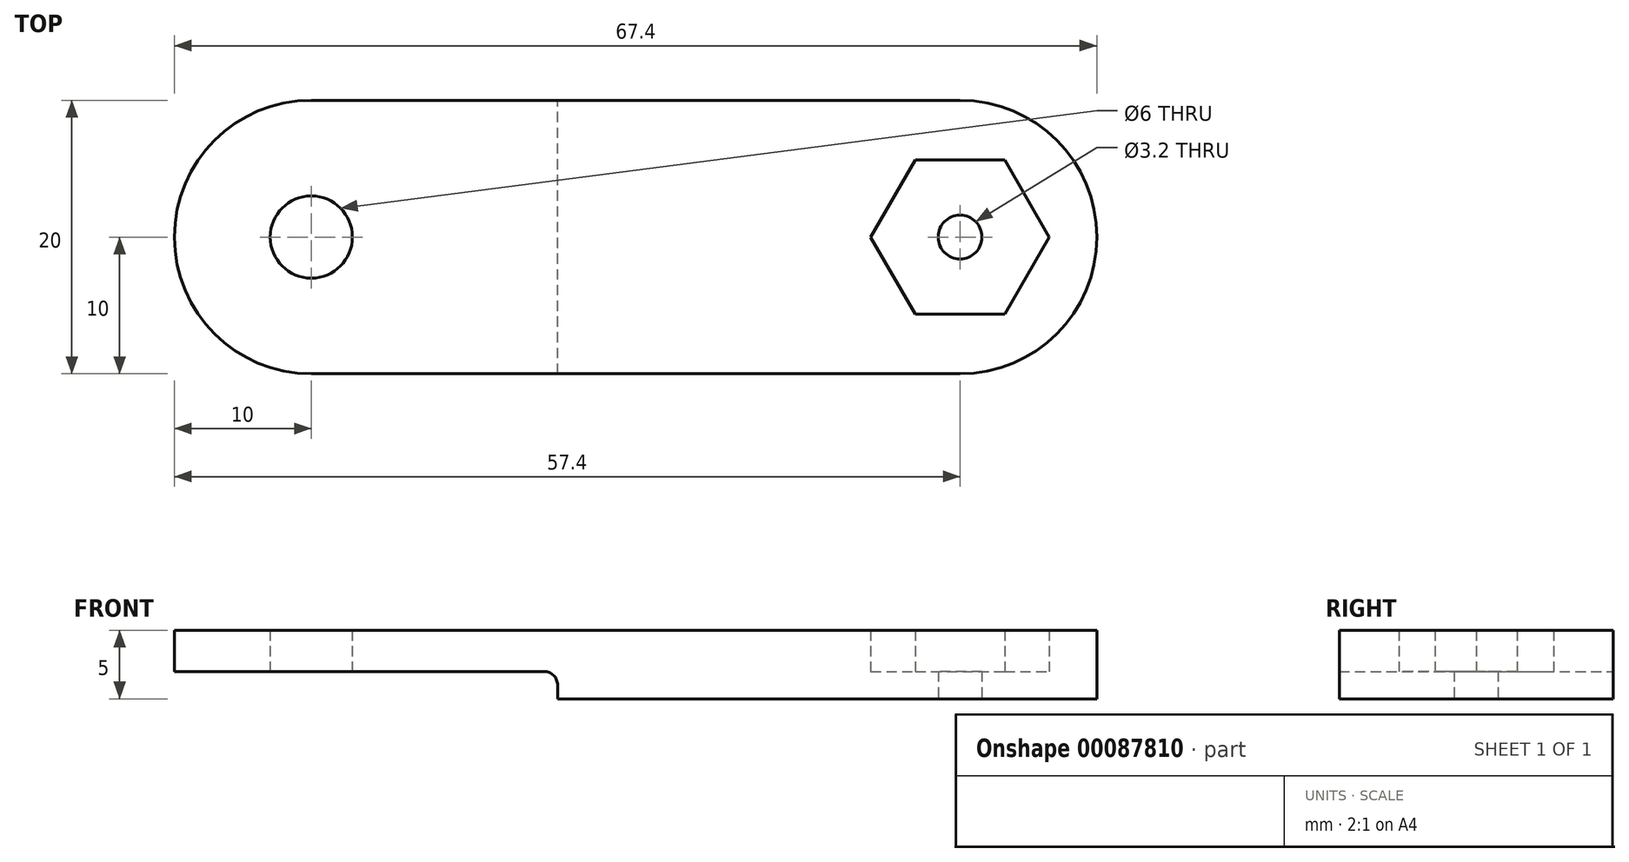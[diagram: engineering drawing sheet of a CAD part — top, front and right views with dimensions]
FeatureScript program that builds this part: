
annotation { "Feature Type Name" : "Feature", "Feature Type Description" : "" }
export const myFeature = defineFeature(function(context is Context, id is Id, definition is map)
    precondition{}
    {
        {
            var Q0;
            Q0=qCreatedBy(makeId("Top.planeOp"),FACE);
            var sketch = newSketch(context, id + "F0", { "sketchPlane" : qUnion([Q0])});
            skArc(sketch, "E0", {"start": v(0, -10) * mm, "mid": v(10, 0) * mm, "end": v(0, 10) * mm});
            skLineSegment(sketch, "E1", {"start": v(0, 10) * mm, "end": v(-47.4, 10) * mm});
            skLineSegment(sketch, "E2", {"start": v(0, -10) * mm, "end": v(-47.4, -10) * mm});
            skArc(sketch, "E3", {"start": v(-47.4, 10) * mm, "mid": v(-57.4, 0) * mm, "end": v(-47.4, -10) * mm});
            skPoint(sketch, "E3.second.point", {"position": v(-47.4, 10) * mm});
            skPoint(sketch, "E3.third.point", {"position": v(-56.72, 3.63) * mm});
            skCircle(sketch, "E4", {"center": v(-47.4, 0) * mm, "radius": 3 * mm});
            skCircle(sketch, "E5.cCircle", {"center": v(0, 0) * mm, "radius": 5.65 * mm, "construction": true});
            skLineSegment(sketch, "E5.0", {"start": v(-3.26, 5.65) * mm, "end": v(3.26, 5.65) * mm});
            skLineSegment(sketch, "E5.1", {"start": v(3.26, 5.65) * mm, "end": v(6.52, 0) * mm});
            skLineSegment(sketch, "E5.2", {"start": v(6.52, 0) * mm, "end": v(3.26, -5.65) * mm});
            skLineSegment(sketch, "E5.3", {"start": v(3.26, -5.65) * mm, "end": v(-3.26, -5.65) * mm});
            skLineSegment(sketch, "E5.4", {"start": v(-3.26, -5.65) * mm, "end": v(-6.52, 0) * mm});
            skLineSegment(sketch, "E5.5", {"start": v(-6.52, 0) * mm, "end": v(-3.26, 5.65) * mm});
            skPoint(sketch, "E5.0.midPoint", {"position": v(0, 5.65) * mm});
            skCircle(sketch, "E6", {"center": v(0, 0) * mm, "radius": 1.6 * mm});
            skSolve(sketch);
        }
        {
            var Q0;
            Q0 = qSketchRegion(id + "F0", true);
            extrude(context, id + "F1", {"entities" : qUnion([Q0]), "depth" : 5 * mm});
        }
        {
            var Q0;
            Q0=makeQuery(id+"F0.imprint","IMPRINT",FACE,{"disambiguationData":[TD([[makeQuery(id+"F0.imprint","IMPRINT",EDGE,{"derivedFrom":sQuery(id+"F0.wireOp",EDGE,"E5.0")}),-1.0]])]});
            extrude(context, id + "F2", {"entities" : qUnion([Q0]), "operationType" : NewBodyOperationType.ADD, "depth" : 2 * mm});
        }
        {
            var Q0;
            Q0=makeQuery(id+"F1.opExtrude","CAP_FACE",FACE,{"disambiguationData":[OSD([sQuery(id+"F0.wireOp",EDGE,"E0"),sQuery(id+"F0.wireOp",EDGE,"E1"),sQuery(id+"F0.wireOp",EDGE,"E2"),sQuery(id+"F0.wireOp",EDGE,"E3"),sQuery(id+"F0.wireOp",EDGE,"E4"),sQuery(id+"F0.wireOp",EDGE,"E5.0"),sQuery(id+"F0.wireOp",EDGE,"E5.1"),sQuery(id+"F0.wireOp",EDGE,"E5.2"),sQuery(id+"F0.wireOp",EDGE,"E5.3"),sQuery(id+"F0.wireOp",EDGE,"E5.4"),sQuery(id+"F0.wireOp",EDGE,"E5.5")])],"isStart":false});
            var sketch = newSketch(context, id + "F3", { "sketchPlane" : qUnion([Q0])});
            skLineSegment(sketch, "E7.bottom", {"start": v(-29.4, 10) * mm, "end": v(-59.4, 10) * mm});
            skLineSegment(sketch, "E7.top", {"start": v(-29.4, -10) * mm, "end": v(-59.4, -10) * mm});
            skLineSegment(sketch, "E7.left", {"start": v(-29.4, 10) * mm, "end": v(-29.4, -10) * mm});
            skLineSegment(sketch, "E7.right", {"start": v(-59.4, 10) * mm, "end": v(-59.4, -10) * mm});
            skLineSegment(sketch, "E8", {"start": v(-47.4, 0) * mm, "end": v(-47.4, 10) * mm, "construction": true});
            skSolve(sketch);
        }
        {
            var Q0;
            {var subQ0=sQuery(id+"F0.wireOp",EDGE,"E5.5");var subQ1=sQuery(id+"F0.wireOp",EDGE,"E5.4");var subQ2=sQuery(id+"F0.wireOp",EDGE,"E5.3");var subQ3=sQuery(id+"F0.wireOp",EDGE,"E5.2");var subQ4=sQuery(id+"F0.wireOp",EDGE,"E5.1");var subQ5=sQuery(id+"F0.wireOp",EDGE,"E5.0");Q0=makeQuery(id+"F2.boolean.opBoolean","MERGE",FACE,{"derivedFrom":[makeQuery(id+"F1.opExtrude","CAP_FACE",FACE,{"disambiguationData":[OSD([sQuery(id+"F0.wireOp",EDGE,"E0"),sQuery(id+"F0.wireOp",EDGE,"E1"),sQuery(id+"F0.wireOp",EDGE,"E2"),sQuery(id+"F0.wireOp",EDGE,"E3"),sQuery(id+"F0.wireOp",EDGE,"E4"),subQ5,subQ4,subQ3,subQ2,subQ1,subQ0])],"isStart":true}),makeQuery(id+"F2.opExtrude","CAP_FACE",FACE,{"disambiguationData":[OSD([subQ5,subQ4,subQ3,subQ2,subQ1,subQ0,sQuery(id+"F0.wireOp",EDGE,"E6")])],"isStart":true})]});}
            var sketch = newSketch(context, id + "F4", { "sketchPlane" : qUnion([Q0])});
            skLineSegment(sketch, "E9.bottom", {"start": v(-29.4, 10) * mm, "end": v(-59.4, 10) * mm});
            skLineSegment(sketch, "E9.top", {"start": v(-29.4, -10) * mm, "end": v(-59.4, -10) * mm});
            skLineSegment(sketch, "E9.left", {"start": v(-29.4, 10) * mm, "end": v(-29.4, -10) * mm});
            skLineSegment(sketch, "E9.right", {"start": v(-59.4, 10) * mm, "end": v(-59.4, -10) * mm});
            skSolve(sketch);
        }
        {
            var Q0;
            Q0 = qSketchRegion(id + "F4", true);
            extrude(context, id + "F5", {"entities" : qUnion([Q0]), "operationType" : NewBodyOperationType.REMOVE, "oppositeDirection" : true, "depth" : 2 * mm});
        }
        {
            var Q0;
            Q0=makeQuery(id+"F5.boolean.opBoolean","COPY",EDGE,{"derivedFrom":makeQuery(id+"F5.opExtrude","CAP_EDGE",EDGE,{"disambiguationData":[OSD([sQuery(id+"F4.wireOp",EDGE,"E9.left")])],"isStart":false})});
            var Q1;
            Q1=makeQuery(id+"F5.boolean.opBoolean","COPY",EDGE,{"derivedFrom":makeQuery(id+"F5.opExtrude","CAP_EDGE",EDGE,{"disambiguationData":[OSD([sQuery(id+"F4.wireOp",EDGE,"E9.left")])],"isStart":true})});
            fillet(context, id + "F6", {"entities" : qUnion([Q0, Q1]), "radius" : 1 * mm, "tangentPropagation" : true, "allowEdgeOverflow" : false});
        }
    });
